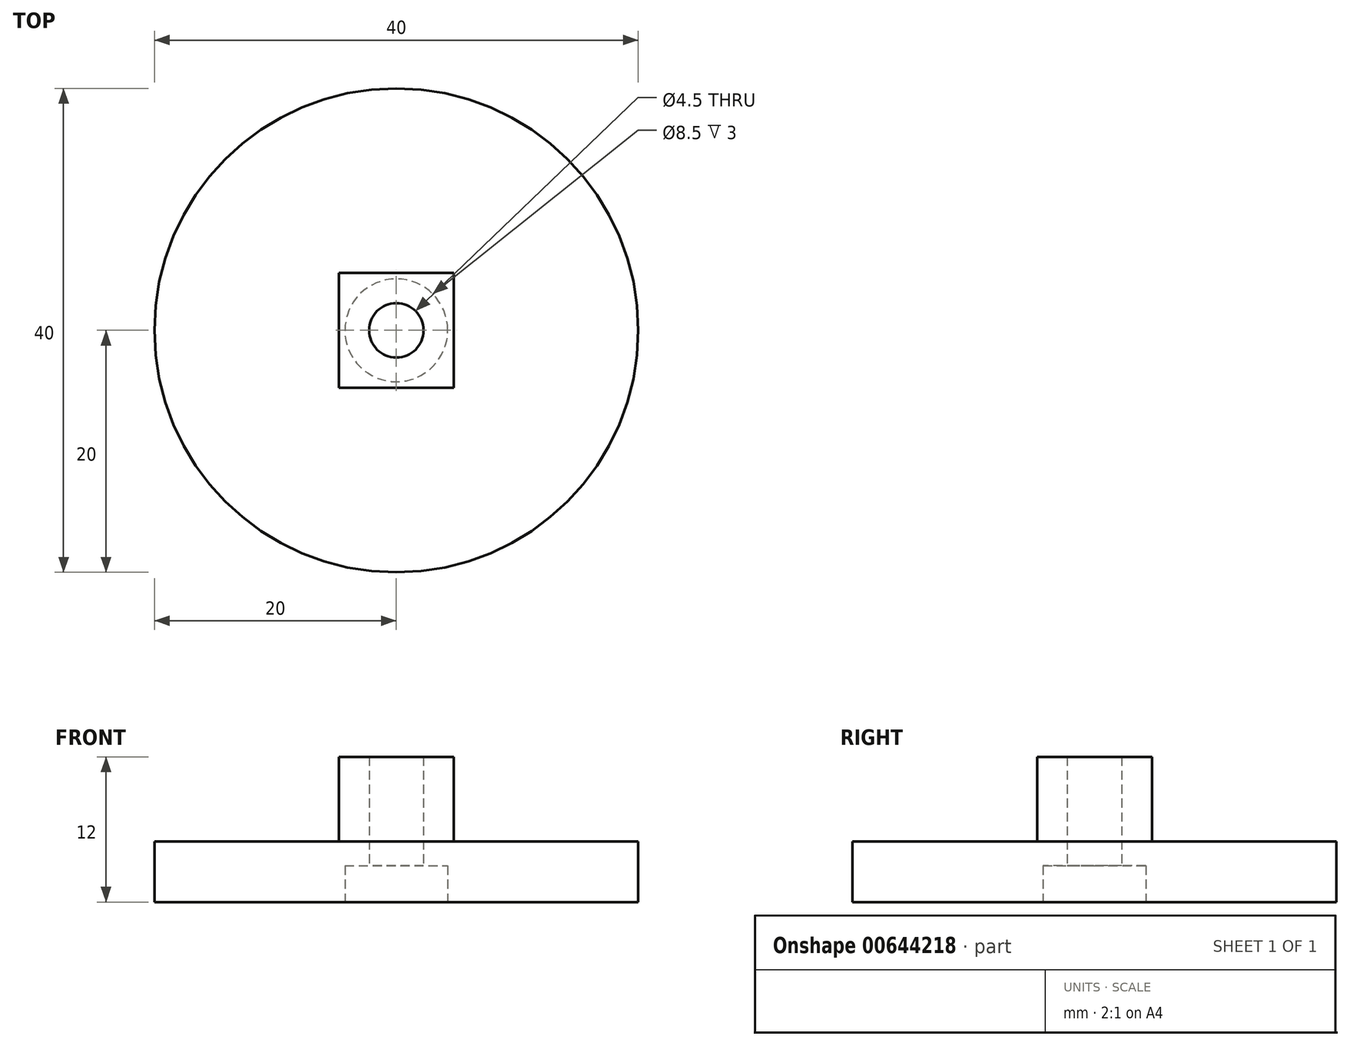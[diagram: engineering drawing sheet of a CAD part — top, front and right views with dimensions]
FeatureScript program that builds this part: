
annotation { "Feature Type Name" : "Feature", "Feature Type Description" : "" }
export const myFeature = defineFeature(function(context is Context, id is Id, definition is map)
    precondition{}
    {
        {
            var Q0;
            Q0=qCreatedBy(makeId("Top.planeOp"),FACE);
            var sketch = newSketch(context, id + "F0", { "sketchPlane" : qUnion([Q0])});
            skCircle(sketch, "E0", {"center": v(0, 0) * mm, "radius": 20 * mm});
            skCircle(sketch, "E1", {"center": v(0, 0) * mm, "radius": 2.25 * mm});
            skSolve(sketch);
        }
        {
            var Q0;
            Q0=makeQuery(id+"F0.imprint","IMPRINT",FACE,{"disambiguationData":[TD([[makeQuery(id+"F0.imprint","IMPRINT",EDGE,{"derivedFrom":sQuery(id+"F0.wireOp",EDGE,"E0")}),1.0]])]});
            extrude(context, id + "F1", {"entities" : qUnion([Q0]), "depth" : 5 * mm, "offsetDistance" : 25 * mm});
        }
        {
            var Q0;
            Q0=makeQuery(id+"F1.opExtrude","CAP_FACE",FACE,{"disambiguationData":[OSD([sQuery(id+"F0.wireOp",EDGE,"E0"),sQuery(id+"F0.wireOp",EDGE,"E1")])],"isStart":false});
            var sketch = newSketch(context, id + "F2", { "sketchPlane" : qUnion([Q0])});
            skLineSegment(sketch, "E2.bottom", {"start": v(4.75, -4.75) * mm, "end": v(-4.75, -4.75) * mm});
            skLineSegment(sketch, "E2.top", {"start": v(4.75, 4.75) * mm, "end": v(-4.75, 4.75) * mm});
            skLineSegment(sketch, "E2.left", {"start": v(4.75, -4.75) * mm, "end": v(4.75, 4.75) * mm});
            skLineSegment(sketch, "E2.right", {"start": v(-4.75, -4.75) * mm, "end": v(-4.75, 4.75) * mm});
            skPoint(sketch, "E2.middle", {"position": v(0, 0) * mm});
            skSolve(sketch);
        }
        {
            var Q0;
            Q0=makeQuery(id+"F2.imprint","IMPRINT",FACE,{"disambiguationData":[TD([[makeQuery(id+"F2.imprint","IMPRINT",EDGE,{"derivedFrom":sQuery(id+"F2.wireOp",EDGE,"E2.bottom")}),-1.0]])]});
            extrude(context, id + "F3", {"entities" : qUnion([Q0]), "operationType" : NewBodyOperationType.ADD, "depth" : 7 * mm, "offsetDistance" : 25 * mm});
        }
        {
            var Q0;
            Q0=makeQuery(id+"F1.opExtrude","CAP_FACE",FACE,{"disambiguationData":[OSD([sQuery(id+"F0.wireOp",EDGE,"E0"),sQuery(id+"F0.wireOp",EDGE,"E1")])],"isStart":true});
            var sketch = newSketch(context, id + "F4", { "sketchPlane" : qUnion([Q0])});
            skCircle(sketch, "E3", {"center": v(0, 0) * mm, "radius": 4.25 * mm});
            skSolve(sketch);
        }
        {
            var Q0;
            Q0=makeQuery(id+"F4.imprint","IMPRINT",FACE,{"disambiguationData":[TD([[makeQuery(id+"F4.imprint","IMPRINT",EDGE,{"derivedFrom":sQuery(id+"F4.wireOp",EDGE,"E3")}),1.0]])]});
            extrude(context, id + "F5", {"entities" : qUnion([Q0]), "operationType" : NewBodyOperationType.REMOVE, "oppositeDirection" : true, "depth" : 3 * mm, "offsetDistance" : 25 * mm});
        }
    });
